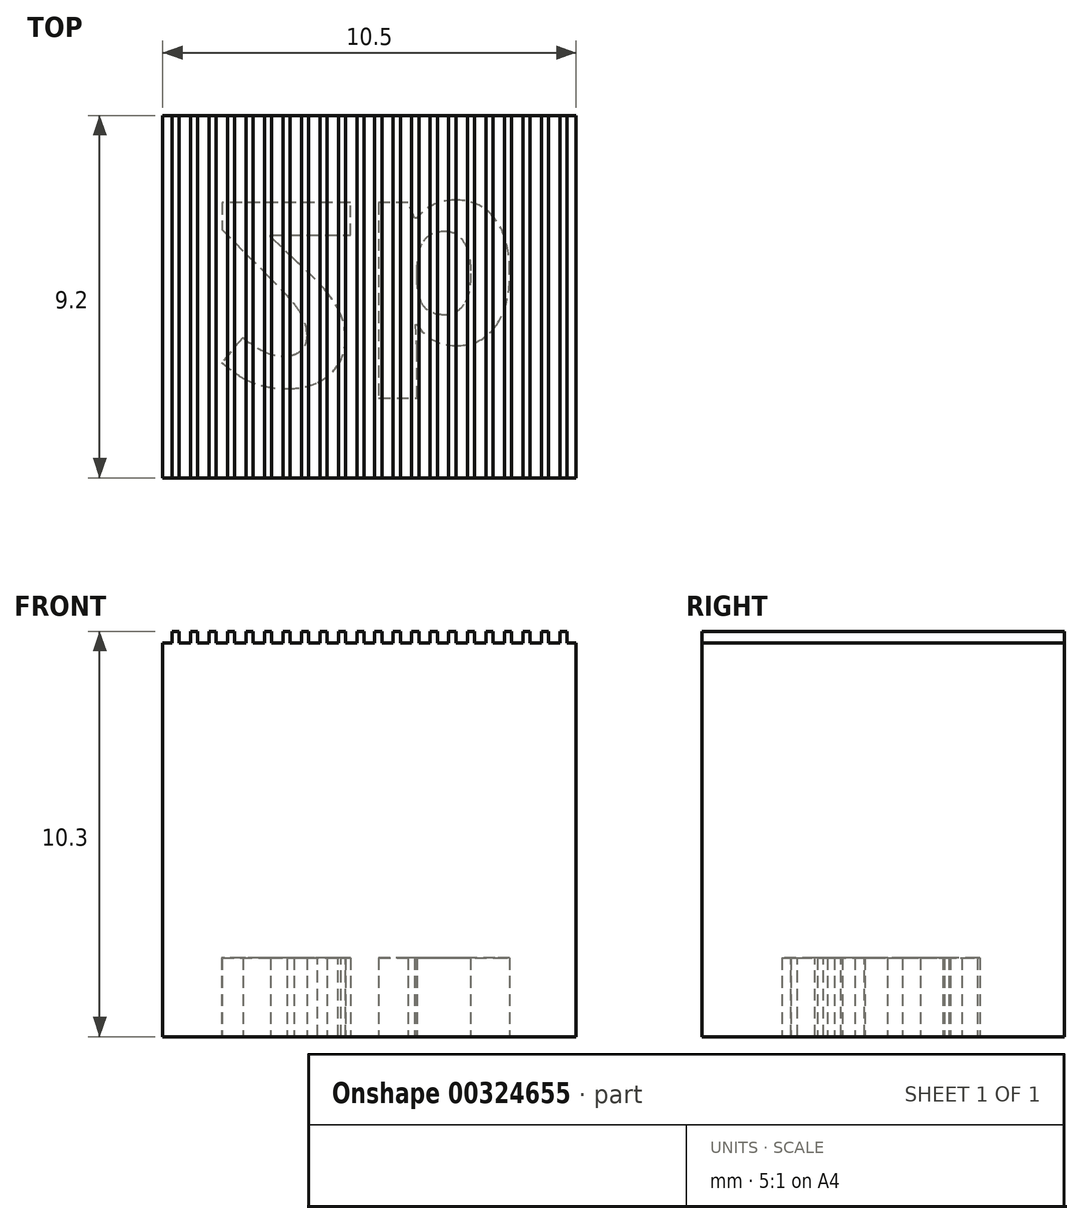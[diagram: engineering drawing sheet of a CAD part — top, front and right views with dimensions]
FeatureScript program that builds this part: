
annotation { "Feature Type Name" : "Feature", "Feature Type Description" : "" }
export const myFeature = defineFeature(function(context is Context, id is Id, definition is map)
    precondition{}
    {
        {
            assignVariable(context, id + "F0", {"name" : "h", "anyValue" : 10});
        }
        {
            assignVariable(context, id + "F1", {"name" : "gh", "anyValue" : 0.3});
        }
        {
            var Q0;
            Q0=qCreatedBy(makeId("Top.planeOp"),FACE);
            var sketch = newSketch(context, id + "F2", { "sketchPlane" : qUnion([Q0])});
            skLineSegment(sketch, "E0.bottom", {"start": v(5.25, 4.6) * mm, "end": v(-5.25, 4.6) * mm});
            skLineSegment(sketch, "E0.top", {"start": v(5.25, -4.6) * mm, "end": v(-5.25, -4.6) * mm});
            skLineSegment(sketch, "E0.left", {"start": v(5.25, 4.6) * mm, "end": v(5.25, -4.6) * mm});
            skLineSegment(sketch, "E0.right", {"start": v(-5.25, 4.6) * mm, "end": v(-5.25, -4.6) * mm});
            skPoint(sketch, "E0.middle", {"position": v(0, 0) * mm});
            skSolve(sketch);
        }
        {
            var Q0;
            Q0=qSketchRegion(id+"F2",true);
            extrude(context, id + "F3", {"entities" : qUnion([Q0]), "depth" : (getVariable(context, 'h')) * mm});
        }
        {
            var Q0;
            Q0=makeQuery(id+"F3.opExtrude","CAP_FACE",FACE,{"disambiguationData":[OSD([sQuery(id+"F2.wireOp",EDGE,"E0.bottom"),sQuery(id+"F2.wireOp",EDGE,"E0.top"),sQuery(id+"F2.wireOp",EDGE,"E0.left"),sQuery(id+"F2.wireOp",EDGE,"E0.right")])],"isStart":false});
            var sketch = newSketch(context, id + "F4", { "sketchPlane" : qUnion([Q0])});
            skLineSegment(sketch, "E1", {"start": v(0.14, 4.6) * mm, "end": v(0.14, -4.6) * mm});
            skLineSegment(sketch, "E2", {"start": v(-0.13, -4.6) * mm, "end": v(-0.14, 4.6) * mm, "construction": true});
            skLineSegment(sketch, "E3", {"start": v(0.32, -4.6) * mm, "end": v(0.31, 4.6) * mm});
            skLineSegment(sketch, "E4", {"start": v(0.14, 0) * mm, "end": v(-0.14, 0) * mm, "construction": true});
            skPoint(sketch, "E5", {"position": v(0, 0) * mm});
            skLineSegment(sketch, "E6", {"start": v(0.13, 4.6) * mm, "end": v(0.32, 4.6) * mm});
            skLineSegment(sketch, "E7", {"start": v(0.32, -4.6) * mm, "end": v(0.13, -4.6) * mm});
            skLineSegment(sketch, "E8.1.0.0", {"start": v(0.6, 4.6) * mm, "end": v(0.79, 4.6) * mm});
            skLineSegment(sketch, "E8.1.0.1", {"start": v(0.79, -4.6) * mm, "end": v(0.79, 4.6) * mm});
            skLineSegment(sketch, "E8.1.0.2", {"start": v(0.6, 4.6) * mm, "end": v(0.6, -4.6) * mm});
            skLineSegment(sketch, "E8.1.0.3", {"start": v(0.79, -4.6) * mm, "end": v(0.6, -4.6) * mm});
            skLineSegment(sketch, "E8.direction1", {"start": v(0.13, 4.6) * mm, "end": v(0.6, 4.6) * mm, "construction": true});
            skLineSegment(sketch, "E9.MirrorCS", {"start": v(-0.14, 0) * mm, "end": v(0.14, 0) * mm, "construction": true});
            skLineSegment(sketch, "E10.MirrorCS", {"start": v(-0.14, 4.6) * mm, "end": v(-0.14, -4.6) * mm});
            skLineSegment(sketch, "E11.MirrorCS", {"start": v(0.14, -4.6) * mm, "end": v(0.13, 4.6) * mm, "construction": true});
            skLineSegment(sketch, "E12.0.2.0", {"start": v(1.08, 4.6) * mm, "end": v(1.26, 4.6) * mm});
            skLineSegment(sketch, "E12.3.2.0", {"start": v(1.26, -4.6) * mm, "end": v(1.26, 4.6) * mm});
            skLineSegment(sketch, "E12.6.2.0", {"start": v(1.08, 4.6) * mm, "end": v(1.08, -4.6) * mm});
            skLineSegment(sketch, "E12.9.2.0", {"start": v(1.26, -4.6) * mm, "end": v(1.08, -4.6) * mm});
            skLineSegment(sketch, "E12.0.3.0", {"start": v(1.55, 4.6) * mm, "end": v(1.73, 4.6) * mm});
            skLineSegment(sketch, "E12.3.3.0", {"start": v(1.73, -4.6) * mm, "end": v(1.73, 4.6) * mm});
            skLineSegment(sketch, "E12.6.3.0", {"start": v(1.55, 4.6) * mm, "end": v(1.55, -4.6) * mm});
            skLineSegment(sketch, "E12.9.3.0", {"start": v(1.73, -4.6) * mm, "end": v(1.55, -4.6) * mm});
            skLineSegment(sketch, "E12.0.4.0", {"start": v(2.02, 4.6) * mm, "end": v(2.2, 4.6) * mm});
            skLineSegment(sketch, "E12.3.4.0", {"start": v(2.2, -4.6) * mm, "end": v(2.2, 4.6) * mm});
            skLineSegment(sketch, "E12.6.4.0", {"start": v(2.02, 4.6) * mm, "end": v(2.02, -4.6) * mm});
            skLineSegment(sketch, "E12.9.4.0", {"start": v(2.2, -4.6) * mm, "end": v(2.02, -4.6) * mm});
            skLineSegment(sketch, "E13.0.5.0", {"start": v(2.49, 4.6) * mm, "end": v(2.67, 4.6) * mm});
            skLineSegment(sketch, "E13.3.5.0", {"start": v(2.67, -4.6) * mm, "end": v(2.67, 4.6) * mm});
            skLineSegment(sketch, "E13.6.5.0", {"start": v(2.49, 4.6) * mm, "end": v(2.49, -4.6) * mm});
            skLineSegment(sketch, "E13.9.5.0", {"start": v(2.67, -4.6) * mm, "end": v(2.49, -4.6) * mm});
            skLineSegment(sketch, "E14.0.6.0", {"start": v(2.96, 4.6) * mm, "end": v(3.14, 4.6) * mm});
            skLineSegment(sketch, "E14.3.6.0", {"start": v(3.14, -4.6) * mm, "end": v(3.14, 4.6) * mm});
            skLineSegment(sketch, "E14.6.6.0", {"start": v(2.96, 4.6) * mm, "end": v(2.96, -4.6) * mm});
            skLineSegment(sketch, "E14.9.6.0", {"start": v(3.14, -4.6) * mm, "end": v(2.96, -4.6) * mm});
            skLineSegment(sketch, "E14.0.7.0", {"start": v(3.43, 4.6) * mm, "end": v(3.6, 4.6) * mm});
            skLineSegment(sketch, "E14.3.7.0", {"start": v(3.6, -4.6) * mm, "end": v(3.6, 4.6) * mm});
            skLineSegment(sketch, "E14.6.7.0", {"start": v(3.43, 4.6) * mm, "end": v(3.43, -4.6) * mm});
            skLineSegment(sketch, "E14.9.7.0", {"start": v(3.6, -4.6) * mm, "end": v(3.43, -4.6) * mm});
            skLineSegment(sketch, "E14.0.8.0", {"start": v(3.9, 4.6) * mm, "end": v(4.08, 4.6) * mm});
            skLineSegment(sketch, "E14.3.8.0", {"start": v(4.08, -4.6) * mm, "end": v(4.08, 4.6) * mm});
            skLineSegment(sketch, "E14.6.8.0", {"start": v(3.9, 4.6) * mm, "end": v(3.9, -4.6) * mm});
            skLineSegment(sketch, "E14.9.8.0", {"start": v(4.08, -4.6) * mm, "end": v(3.9, -4.6) * mm});
            skLineSegment(sketch, "E14.0.9.0", {"start": v(4.37, 4.6) * mm, "end": v(4.55, 4.6) * mm});
            skLineSegment(sketch, "E14.3.9.0", {"start": v(4.55, -4.6) * mm, "end": v(4.55, 4.6) * mm});
            skLineSegment(sketch, "E14.6.9.0", {"start": v(4.37, 4.6) * mm, "end": v(4.37, -4.6) * mm});
            skLineSegment(sketch, "E14.9.9.0", {"start": v(4.55, -4.6) * mm, "end": v(4.37, -4.6) * mm});
            skLineSegment(sketch, "E14.0.10.0", {"start": v(4.84, 4.6) * mm, "end": v(5.02, 4.6) * mm});
            skLineSegment(sketch, "E14.3.10.0", {"start": v(5.02, -4.6) * mm, "end": v(5.02, 4.6) * mm});
            skLineSegment(sketch, "E14.6.10.0", {"start": v(4.84, 4.6) * mm, "end": v(4.84, -4.6) * mm});
            skLineSegment(sketch, "E14.9.10.0", {"start": v(5.02, -4.6) * mm, "end": v(4.84, -4.6) * mm});
            skLineSegment(sketch, "E15.MirrorCS", {"start": v(-0.13, 4.6) * mm, "end": v(-0.32, 4.6) * mm});
            skLineSegment(sketch, "E16.MirrorCS", {"start": v(-4.37, 4.6) * mm, "end": v(-4.55, 4.6) * mm});
            skLineSegment(sketch, "E17.MirrorCS", {"start": v(-4.84, 4.6) * mm, "end": v(-5.02, 4.6) * mm});
            skLineSegment(sketch, "E18.MirrorCS", {"start": v(-0.13, 4.6) * mm, "end": v(-0.6, 4.6) * mm, "construction": true});
            skLineSegment(sketch, "E19.MirrorCS", {"start": v(-2.96, 4.6) * mm, "end": v(-3.14, 4.6) * mm});
            skLineSegment(sketch, "E20.MirrorCS", {"start": v(-2.02, 4.6) * mm, "end": v(-2.2, 4.6) * mm});
            skLineSegment(sketch, "E21.MirrorCS", {"start": v(-2.49, 4.6) * mm, "end": v(-2.67, 4.6) * mm});
            skLineSegment(sketch, "E22.MirrorCS", {"start": v(-1.08, 4.6) * mm, "end": v(-1.26, 4.6) * mm});
            skLineSegment(sketch, "E23.MirrorCS", {"start": v(-3.9, 4.6) * mm, "end": v(-4.08, 4.6) * mm});
            skLineSegment(sketch, "E24.MirrorCS", {"start": v(-0.6, 4.6) * mm, "end": v(-0.79, 4.6) * mm});
            skLineSegment(sketch, "E25.MirrorCS", {"start": v(-3.43, 4.6) * mm, "end": v(-3.6, 4.6) * mm});
            skLineSegment(sketch, "E26.MirrorCS", {"start": v(-1.55, 4.6) * mm, "end": v(-1.73, 4.6) * mm});
            skLineSegment(sketch, "E27.MirrorCS", {"start": v(-0.31, -4.6) * mm, "end": v(-0.32, 4.6) * mm});
            skLineSegment(sketch, "E28.MirrorCS", {"start": v(-0.6, 4.6) * mm, "end": v(-0.6, -4.6) * mm});
            skLineSegment(sketch, "E29.MirrorCS", {"start": v(-0.79, -4.6) * mm, "end": v(-0.79, 4.6) * mm});
            skLineSegment(sketch, "E30.MirrorCS", {"start": v(-1.08, 4.6) * mm, "end": v(-1.08, -4.6) * mm});
            skLineSegment(sketch, "E31.MirrorCS", {"start": v(-1.26, -4.6) * mm, "end": v(-1.26, 4.6) * mm});
            skLineSegment(sketch, "E32.MirrorCS", {"start": v(-1.55, 4.6) * mm, "end": v(-1.55, -4.6) * mm});
            skLineSegment(sketch, "E33.MirrorCS", {"start": v(-1.73, -4.6) * mm, "end": v(-1.73, 4.6) * mm});
            skLineSegment(sketch, "E34.MirrorCS", {"start": v(-2.02, 4.6) * mm, "end": v(-2.02, -4.6) * mm});
            skLineSegment(sketch, "E35.MirrorCS", {"start": v(-2.2, -4.6) * mm, "end": v(-2.2, 4.6) * mm});
            skLineSegment(sketch, "E36.MirrorCS", {"start": v(-2.49, 4.6) * mm, "end": v(-2.49, -4.6) * mm});
            skLineSegment(sketch, "E37.MirrorCS", {"start": v(-2.67, -4.6) * mm, "end": v(-2.67, 4.6) * mm});
            skLineSegment(sketch, "E38.MirrorCS", {"start": v(-2.96, 4.6) * mm, "end": v(-2.96, -4.6) * mm});
            skLineSegment(sketch, "E39.MirrorCS", {"start": v(-3.14, -4.6) * mm, "end": v(-3.14, 4.6) * mm});
            skLineSegment(sketch, "E40.MirrorCS", {"start": v(-3.43, 4.6) * mm, "end": v(-3.43, -4.6) * mm});
            skLineSegment(sketch, "E41.MirrorCS", {"start": v(-3.6, -4.6) * mm, "end": v(-3.6, 4.6) * mm});
            skLineSegment(sketch, "E42.MirrorCS", {"start": v(-3.9, 4.6) * mm, "end": v(-3.9, -4.6) * mm});
            skLineSegment(sketch, "E43.MirrorCS", {"start": v(-4.08, -4.6) * mm, "end": v(-4.08, 4.6) * mm});
            skLineSegment(sketch, "E44.MirrorCS", {"start": v(-4.37, 4.6) * mm, "end": v(-4.37, -4.6) * mm});
            skLineSegment(sketch, "E45.MirrorCS", {"start": v(-4.55, -4.6) * mm, "end": v(-4.55, 4.6) * mm});
            skLineSegment(sketch, "E46.MirrorCS", {"start": v(-4.84, 4.6) * mm, "end": v(-4.84, -4.6) * mm});
            skLineSegment(sketch, "E47.MirrorCS", {"start": v(-5.02, -4.6) * mm, "end": v(-5.02, 4.6) * mm});
            skLineSegment(sketch, "E48.MirrorCS", {"start": v(-0.32, -4.6) * mm, "end": v(-0.13, -4.6) * mm});
            skLineSegment(sketch, "E49.MirrorCS", {"start": v(-1.26, -4.6) * mm, "end": v(-1.08, -4.6) * mm});
            skLineSegment(sketch, "E50.MirrorCS", {"start": v(-3.14, -4.6) * mm, "end": v(-2.96, -4.6) * mm});
            skLineSegment(sketch, "E51.MirrorCS", {"start": v(-1.73, -4.6) * mm, "end": v(-1.55, -4.6) * mm});
            skLineSegment(sketch, "E52.MirrorCS", {"start": v(-4.08, -4.6) * mm, "end": v(-3.9, -4.6) * mm});
            skLineSegment(sketch, "E53.MirrorCS", {"start": v(-3.6, -4.6) * mm, "end": v(-3.43, -4.6) * mm});
            skLineSegment(sketch, "E54.MirrorCS", {"start": v(-5.02, -4.6) * mm, "end": v(-4.84, -4.6) * mm});
            skLineSegment(sketch, "E55.MirrorCS", {"start": v(-0.79, -4.6) * mm, "end": v(-0.6, -4.6) * mm});
            skLineSegment(sketch, "E56.MirrorCS", {"start": v(-2.67, -4.6) * mm, "end": v(-2.49, -4.6) * mm});
            skLineSegment(sketch, "E57.MirrorCS", {"start": v(-4.55, -4.6) * mm, "end": v(-4.37, -4.6) * mm});
            skLineSegment(sketch, "E58.MirrorCS", {"start": v(-2.2, -4.6) * mm, "end": v(-2.02, -4.6) * mm});
            skSolve(sketch);
        }
        {
            var Q0;
            Q0=qSketchRegion(id+"F4",true);
            extrude(context, id + "F5", {"entities" : qUnion([Q0]), "operationType" : NewBodyOperationType.ADD, "depth" : (getVariable(context, 'gh')) * mm});
        }
        {
            var Q0;
            Q0=qSketchRegion(id+"F4",true);
            extrude(context, id + "F6", {"entities" : qUnion([Q0]), "operationType" : NewBodyOperationType.ADD, "depth" : (getVariable(context, 'gh')) * mm});
        }
        {
            var Q0;
            Q0=makeQuery(id+"F3.opExtrude","CAP_FACE",FACE,{"disambiguationData":[OSD([sQuery(id+"F2.wireOp",EDGE,"E0.bottom"),sQuery(id+"F2.wireOp",EDGE,"E0.top"),sQuery(id+"F2.wireOp",EDGE,"E0.left"),sQuery(id+"F2.wireOp",EDGE,"E0.right")])],"isStart":true});
            var sketch = newSketch(context, id + "F7", { "sketchPlane" : qUnion([Q0])});
            skText(sketch, "E59", { "text": "2b", "fontName": "OpenSans-Bold.ttf"});
            const initialGuessF7  = {"E59": [-0.004, -0.00239, 1, 0, 0.0047]};
            skSetInitialGuess(sketch, initialGuessF7);
            skSolve(sketch);
        }
        {
            var Q0;
            Q0=qSketchRegion(id+"F7",true);
            extrude(context, id + "F8", {"entities" : qUnion([Q0]), "operationType" : NewBodyOperationType.REMOVE, "oppositeDirection" : true, "depth" : 2 * mm});
        }
    });
